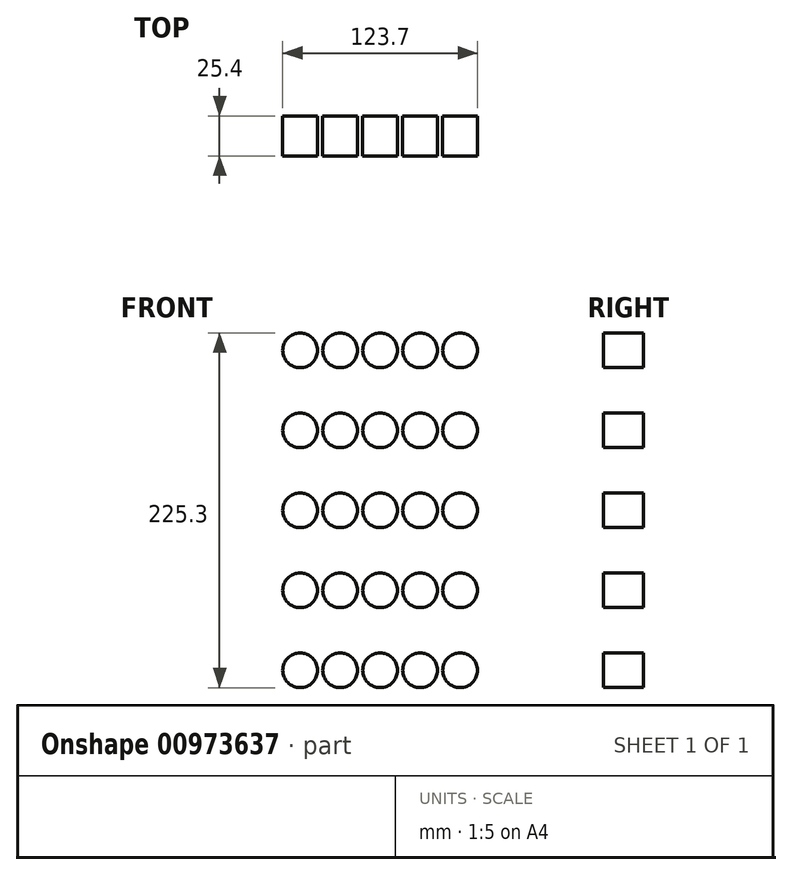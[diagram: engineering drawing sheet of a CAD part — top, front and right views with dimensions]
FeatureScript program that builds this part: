
annotation { "Feature Type Name" : "Feature", "Feature Type Description" : "" }
export const myFeature = defineFeature(function(context is Context, id is Id, definition is map)
    precondition{}
    {
        {
            var Q0;
            Q0=qCreatedBy(makeId("Front.planeOp"),FACE);
            var sketch = newSketch(context, id + "F0", { "sketchPlane" : qUnion([Q0])});
            skCircle(sketch, "E0", {"center": v(-36.63, 35) * mm, "radius": 11.05 * mm});
            skCircle(sketch, "E1.0.1.0", {"center": v(-36.63, -15.8) * mm, "radius": 11.05 * mm});
            skCircle(sketch, "E1.0.2.0", {"center": v(-36.63, -66.6) * mm, "radius": 11.05 * mm});
            skCircle(sketch, "E1.0.3.0", {"center": v(-36.63, -117.4) * mm, "radius": 11.05 * mm});
            skCircle(sketch, "E1.0.4.0", {"center": v(-36.63, -168.2) * mm, "radius": 11.05 * mm});
            skCircle(sketch, "E1.1.0.0", {"center": v(-11.23, 35) * mm, "radius": 11.05 * mm});
            skCircle(sketch, "E1.1.1.0", {"center": v(-11.23, -15.8) * mm, "radius": 11.05 * mm});
            skCircle(sketch, "E1.1.2.0", {"center": v(-11.23, -66.6) * mm, "radius": 11.05 * mm});
            skCircle(sketch, "E1.1.3.0", {"center": v(-11.23, -117.4) * mm, "radius": 11.05 * mm});
            skCircle(sketch, "E1.1.4.0", {"center": v(-11.23, -168.2) * mm, "radius": 11.05 * mm});
            skCircle(sketch, "E1.2.0.0", {"center": v(14.17, 35) * mm, "radius": 11.05 * mm});
            skCircle(sketch, "E1.2.1.0", {"center": v(14.17, -15.8) * mm, "radius": 11.05 * mm});
            skCircle(sketch, "E1.2.2.0", {"center": v(14.17, -66.6) * mm, "radius": 11.05 * mm});
            skCircle(sketch, "E1.2.3.0", {"center": v(14.17, -117.4) * mm, "radius": 11.05 * mm});
            skCircle(sketch, "E1.2.4.0", {"center": v(14.17, -168.2) * mm, "radius": 11.05 * mm});
            skCircle(sketch, "E1.3.0.0", {"center": v(39.57, 35) * mm, "radius": 11.05 * mm});
            skCircle(sketch, "E1.3.1.0", {"center": v(39.57, -15.8) * mm, "radius": 11.05 * mm});
            skCircle(sketch, "E1.3.2.0", {"center": v(39.57, -66.6) * mm, "radius": 11.05 * mm});
            skCircle(sketch, "E1.3.3.0", {"center": v(39.57, -117.4) * mm, "radius": 11.05 * mm});
            skCircle(sketch, "E1.3.4.0", {"center": v(39.57, -168.2) * mm, "radius": 11.05 * mm});
            skCircle(sketch, "E1.4.0.0", {"center": v(64.97, 35) * mm, "radius": 11.05 * mm});
            skCircle(sketch, "E1.4.1.0", {"center": v(64.97, -15.8) * mm, "radius": 11.05 * mm});
            skCircle(sketch, "E1.4.2.0", {"center": v(64.97, -66.6) * mm, "radius": 11.05 * mm});
            skCircle(sketch, "E1.4.3.0", {"center": v(64.97, -117.4) * mm, "radius": 11.05 * mm});
            skCircle(sketch, "E1.4.4.0", {"center": v(64.97, -168.2) * mm, "radius": 11.05 * mm});
            skLineSegment(sketch, "E1.direction1", {"start": v(-36.63, 35) * mm, "end": v(-11.23, 35) * mm, "construction": true});
            skLineSegment(sketch, "E1.direction2", {"start": v(-36.63, 35) * mm, "end": v(-36.63, -15.8) * mm, "construction": true});
            skSolve(sketch);
        }
        {
            var Q0;
            Q0 = qSketchRegion(id + "F0", true);
            extrude(context, id + "F1", {"entities" : qUnion([Q0]), "depth" : 25.4 * mm, "offsetDistance" : 25.4 * mm});
        }
    });
